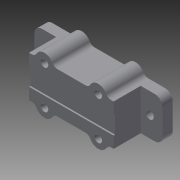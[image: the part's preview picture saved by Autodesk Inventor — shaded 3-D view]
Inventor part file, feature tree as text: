
AUTODESK INVENTOR PART (.ipt)
format: ipt  version: 2015 (Build 190159000, 159)  size: 170,496 bytes
history: native  units: mm
features: sketch x4, extrude x3, hole x2, fillet x2
ambient origin geometry x8: Origin, YZ Plane, XZ Plane, XY Plane, X Axis, Y Axis, Z Axis, Center Point
bodies: Body1 (feature_tree)
feature tree (11):
  sketch  "Sketch1"  dims[d0=16.0mm d1=50.0mm]
  extrude  "Extrusion2"  Depth=50.0mm
  extrude  "Extrusion3"  Depth=7.0mm
  hole  "Hole1"  [1 undecoded]
  hole  "Hole2"  [1 undecoded]
  fillet  "Fillet1"  Radius=2.0mm
  fillet  "Fillet2"  Radius=3.0mm
  extrude  "Extrusion4"  Depth=0.6mm
  sketch  "Sketch2"  dims[d4=21.0mm d5=7.0mm]
  sketch  "Sketch3"  dims[d6=14.6mm d7=0.0mm d8=8.5mm]
  sketch  "Sketch4"  dims[d9=10.6mm d10=0.0mm d12=20.0mm d13=3.2mm d14=6.0mm d15=4.0mm d16=2.0mm d17=45.0deg d18=8.0mm d19=20.594885mm d20=2.4mm d21=6.0mm d22=3.0mm d23=2.0mm d24=45.0deg d25=8.0mm d26=20.594885mm d27=2.0mm d28=3.0mm d31=15.0mm d32=7.0mm d33=0.6mm d34=0.0mm]
note: 2 required parameter values undecoded (feature->parameter linkage not recoverable at this tier; creation-order binding heuristic only, values carry confidence <= 0.55)
